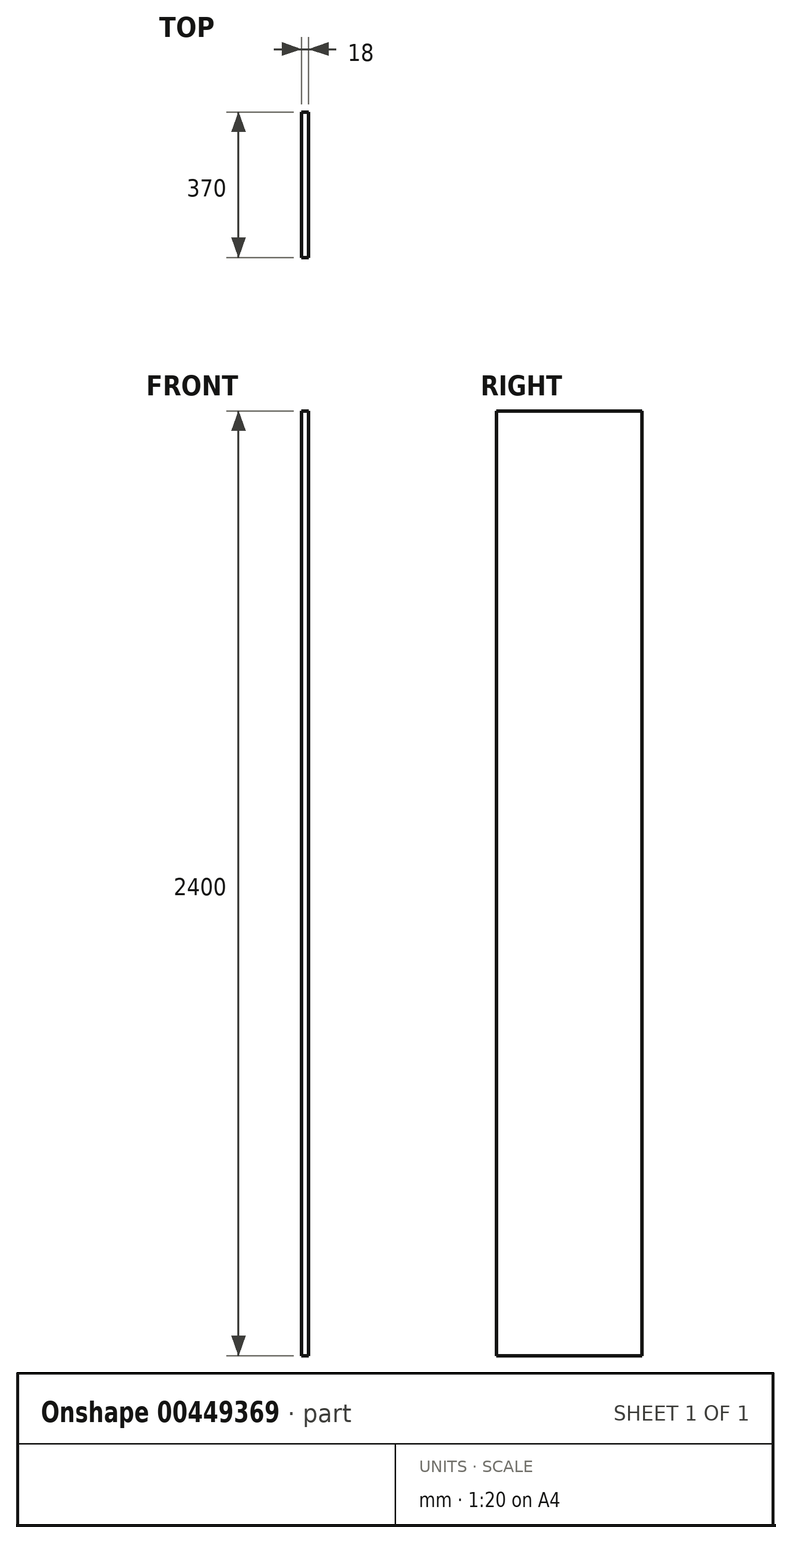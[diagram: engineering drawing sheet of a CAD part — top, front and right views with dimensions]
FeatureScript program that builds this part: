
annotation { "Feature Type Name" : "Feature", "Feature Type Description" : "" }
export const myFeature = defineFeature(function(context is Context, id is Id, definition is map)
    precondition{}
    {
        {
            var Q0;
            Q0=qCreatedBy(makeId("Right.planeOp"),FACE);
            var sketch = newSketch(context, id + "F0", { "sketchPlane" : qUnion([Q0])});
            skLineSegment(sketch, "E0.bottom", {"start": v(0, 0) * mm, "end": v(370, 0) * mm});
            skLineSegment(sketch, "E0.top", {"start": v(0, 2400) * mm, "end": v(370, 2400) * mm});
            skLineSegment(sketch, "E0.left", {"start": v(0, 0) * mm, "end": v(0, 2400) * mm});
            skLineSegment(sketch, "E0.right", {"start": v(370, 0) * mm, "end": v(370, 2400) * mm});
            skSolve(sketch);
        }
        {
            var Q0;
            Q0 = qSketchRegion(id + "F0", true);
            extrude(context, id + "F1", {"entities" : qUnion([Q0]), "depth" : 18 * mm, "offsetDistance" : 25 * mm});
        }
    });
